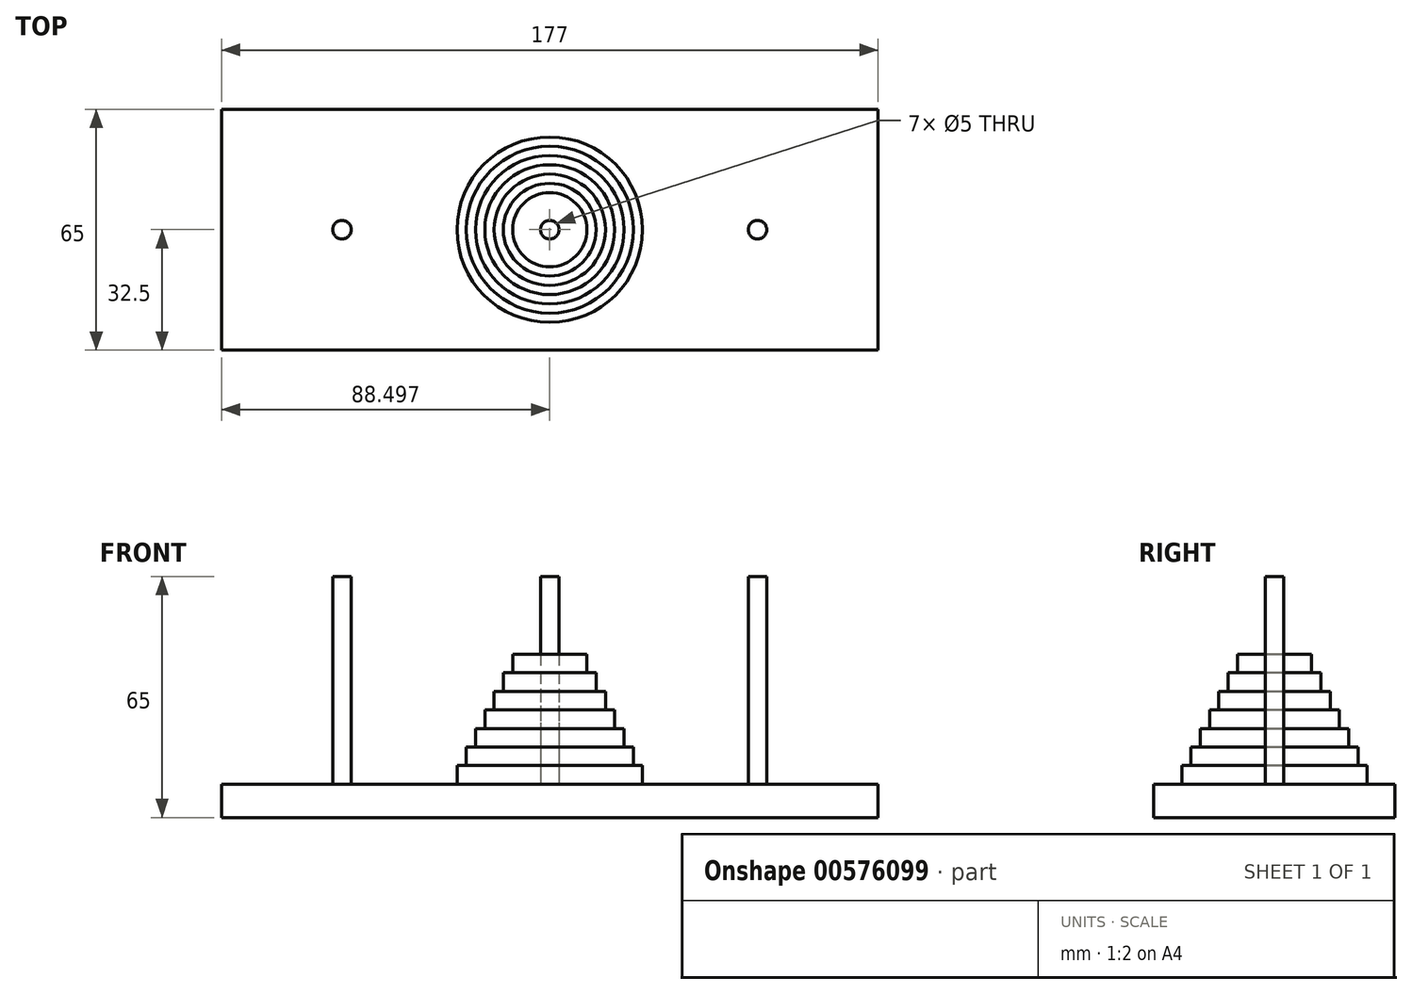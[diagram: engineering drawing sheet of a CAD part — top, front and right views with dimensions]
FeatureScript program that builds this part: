
annotation { "Feature Type Name" : "Feature", "Feature Type Description" : "" }
export const myFeature = defineFeature(function(context is Context, id is Id, definition is map)
    precondition{}
    {
        {
            var Q0;
            Q0=qCreatedBy(makeId("Front.planeOp"),FACE);
            var sketch = newSketch(context, id + "F0", { "sketchPlane" : qUnion([Q0])});
            skLineSegment(sketch, "E0", {"start": v(-126.76, 11.57) * mm, "end": v(50.24, 11.57) * mm});
            skLineSegment(sketch, "E1", {"start": v(50.24, 11.57) * mm, "end": v(50.24, 20.57) * mm});
            skLineSegment(sketch, "E2", {"start": v(50.24, 20.57) * mm, "end": v(-126.76, 20.57) * mm});
            skLineSegment(sketch, "E3", {"start": v(-126.76, 20.57) * mm, "end": v(-126.76, 11.57) * mm});
            skSolve(sketch);
        }
        {
            var Q0;
            Q0=makeQuery(id+"F0.imprint","IMPRINT",FACE,{"disambiguationData":[TD([[makeQuery(id+"F0.imprint","IMPRINT",EDGE,{"derivedFrom":sQuery(id+"F0.wireOp",EDGE,"E0")}),1.0]])]});
            extrude(context, id + "F1", {"entities" : qUnion([Q0]), "depth" : 65 * mm, "offsetDistance" : 25.4 * mm});
        }
        {
            var Q0;
            Q0=makeQuery(id+"F1.opExtrude","SWEPT_FACE",FACE,{"disambiguationData":[OSD([sQuery(id+"F0.wireOp",EDGE,"E2")])]});
            var sketch = newSketch(context, id + "F2", { "sketchPlane" : qUnion([Q0])});
            skLineSegment(sketch, "E4", {"start": v(20.24, -32.5) * mm, "end": v(17.74, -32.5) * mm});
            skLineSegment(sketch, "E5", {"start": v(17.74, -32.5) * mm, "end": v(15.24, -32.5) * mm});
            skLineSegment(sketch, "E6", {"start": v(-38.26, -32.5) * mm, "end": v(-40.76, -32.5) * mm});
            skLineSegment(sketch, "E7", {"start": v(-94.26, -32.5) * mm, "end": v(-96.76, -32.5) * mm});
            skCircle(sketch, "E8", {"center": v(-94.26, -32.5) * mm, "radius": 2.5 * mm});
            skCircle(sketch, "E9", {"center": v(-38.26, -32.5) * mm, "radius": 2.5 * mm});
            skCircle(sketch, "E10", {"center": v(17.74, -32.5) * mm, "radius": 2.5 * mm});
            skLineSegment(sketch, "E11.trimOffspring", {"start": v(-91.76, -32.5) * mm, "end": v(-94.26, -32.5) * mm});
            skPoint(sketch, "E12.orphan", {"position": v(-126.76, -32.5) * mm});
            skLineSegment(sketch, "E13.trimOffspring", {"start": v(-35.76, -32.5) * mm, "end": v(-38.26, -32.5) * mm});
            skPoint(sketch, "E14.orphan", {"position": v(50.24, -32.5) * mm});
            skSolve(sketch);
        }
        {
            var Q0;
            Q0 = qSketchRegion(id + "F2", true);
            extrude(context, id + "F3", {"entities" : qUnion([Q0]), "operationType" : NewBodyOperationType.ADD, "depth" : 56 * mm, "offsetDistance" : 25.4 * mm});
        }
        {
            var Q0;
            Q0=makeQuery(id+"F1.opExtrude","SWEPT_FACE",FACE,{"disambiguationData":[OSD([sQuery(id+"F0.wireOp",EDGE,"E2")])]});
            var sketch = newSketch(context, id + "F4", { "sketchPlane" : qUnion([Q0])});
            skCircle(sketch, "E15", {"center": v(-38.26, -32.5) * mm, "radius": 25 * mm});
            skLineSegment(sketch, "E16", {"start": v(-38.26, -32.5) * mm, "end": v(-38.26, -57.5) * mm});
            skLineSegment(sketch, "E17", {"start": v(-38.26, -57.5) * mm, "end": v(-38.26, -7.5) * mm});
            skSolve(sketch);
        }
        {
            var Q0;
            Q0=makeQuery(id+"F4.imprint","IMPRINT",FACE,{"disambiguationData":[TD([[makeQuery(id+"F4.imprint","IMPRINT",EDGE,{"derivedFrom":sQuery(id+"F4.wireOp",EDGE,"E15")}),1.0]])]});
            extrude(context, id + "F5", {"entities" : qUnion([Q0]), "depth" : 5 * mm, "offsetDistance" : 25.4 * mm});
        }
        {
            var Q0;
            Q0=makeQuery(id+"F5.opExtrude","CAP_FACE",FACE,{"disambiguationData":[OSD([sQuery(id+"F2.wireOp",EDGE,"E9"),sQuery(id+"F4.wireOp",EDGE,"E15")])],"isStart":false});
            var sketch = newSketch(context, id + "F6", { "sketchPlane" : qUnion([Q0])});
            skCircle(sketch, "E18", {"center": v(-38.26, -32.5) * mm, "radius": 22.5 * mm});
            skSolve(sketch);
        }
        {
            var Q0;
            Q0=makeQuery(id+"F6.imprint","IMPRINT",FACE,{"disambiguationData":[TD([[makeQuery(id+"F6.imprint","IMPRINT",EDGE,{"derivedFrom":sQuery(id+"F6.wireOp",EDGE,"E18")}),1.0]])]});
            extrude(context, id + "F7", {"entities" : qUnion([Q0]), "depth" : 5 * mm, "offsetDistance" : 25.4 * mm});
        }
        {
            var Q0;
            Q0=makeQuery(id+"F7.opExtrude","CAP_FACE",FACE,{"disambiguationData":[OSD([sQuery(id+"F2.wireOp",EDGE,"E9"),sQuery(id+"F6.wireOp",EDGE,"E18")])],"isStart":false});
            var sketch = newSketch(context, id + "F8", { "sketchPlane" : qUnion([Q0])});
            skCircle(sketch, "E19", {"center": v(-38.26, -32.5) * mm, "radius": 20 * mm});
            skSolve(sketch);
        }
        {
            var Q0;
            Q0=makeQuery(id+"F8.imprint","IMPRINT",FACE,{"disambiguationData":[TD([[makeQuery(id+"F8.imprint","IMPRINT",EDGE,{"derivedFrom":sQuery(id+"F8.wireOp",EDGE,"E19")}),1.0]])]});
            extrude(context, id + "F9", {"entities" : qUnion([Q0]), "depth" : 5 * mm, "offsetDistance" : 25.4 * mm});
        }
        {
            var Q0;
            Q0=makeQuery(id+"F9.opExtrude","CAP_FACE",FACE,{"disambiguationData":[OSD([sQuery(id+"F2.wireOp",EDGE,"E9"),sQuery(id+"F8.wireOp",EDGE,"E19")])],"isStart":false});
            var sketch = newSketch(context, id + "F10", { "sketchPlane" : qUnion([Q0])});
            skCircle(sketch, "E20", {"center": v(-38.26, -32.5) * mm, "radius": 17.5 * mm});
            skSolve(sketch);
        }
        {
            var Q0;
            Q0=makeQuery(id+"F10.imprint","IMPRINT",FACE,{"disambiguationData":[TD([[makeQuery(id+"F10.imprint","IMPRINT",EDGE,{"derivedFrom":sQuery(id+"F10.wireOp",EDGE,"E20")}),1.0]])]});
            extrude(context, id + "F11", {"entities" : qUnion([Q0]), "depth" : 5 * mm, "offsetDistance" : 25.4 * mm});
        }
        {
            var Q0;
            Q0=makeQuery(id+"F11.opExtrude","CAP_FACE",FACE,{"disambiguationData":[OSD([sQuery(id+"F2.wireOp",EDGE,"E9"),sQuery(id+"F10.wireOp",EDGE,"E20")])],"isStart":false});
            var sketch = newSketch(context, id + "F12", { "sketchPlane" : qUnion([Q0])});
            skCircle(sketch, "E21", {"center": v(-38.26, -32.5) * mm, "radius": 15 * mm});
            skSolve(sketch);
        }
        {
            var Q0;
            Q0=makeQuery(id+"F12.imprint","IMPRINT",FACE,{"disambiguationData":[TD([[makeQuery(id+"F12.imprint","IMPRINT",EDGE,{"derivedFrom":sQuery(id+"F12.wireOp",EDGE,"E21")}),1.0]])]});
            extrude(context, id + "F13", {"entities" : qUnion([Q0]), "depth" : 5 * mm, "offsetDistance" : 25.4 * mm});
        }
        {
            var Q0;
            Q0=makeQuery(id+"F13.opExtrude","CAP_FACE",FACE,{"disambiguationData":[OSD([sQuery(id+"F2.wireOp",EDGE,"E9"),sQuery(id+"F12.wireOp",EDGE,"E21")])],"isStart":false});
            var sketch = newSketch(context, id + "F14", { "sketchPlane" : qUnion([Q0])});
            skCircle(sketch, "E22", {"center": v(-38.26, -32.5) * mm, "radius": 12.5 * mm});
            skSolve(sketch);
        }
        {
            var Q0;
            Q0=makeQuery(id+"F14.imprint","IMPRINT",FACE,{"disambiguationData":[TD([[makeQuery(id+"F14.imprint","IMPRINT",EDGE,{"derivedFrom":sQuery(id+"F14.wireOp",EDGE,"E22")}),1.0]])]});
            extrude(context, id + "F15", {"entities" : qUnion([Q0]), "depth" : 5 * mm, "offsetDistance" : 25.4 * mm});
        }
        {
            var Q0;
            Q0=makeQuery(id+"F15.opExtrude","CAP_FACE",FACE,{"disambiguationData":[OSD([sQuery(id+"F2.wireOp",EDGE,"E9"),sQuery(id+"F14.wireOp",EDGE,"E22")])],"isStart":false});
            var sketch = newSketch(context, id + "F16", { "sketchPlane" : qUnion([Q0])});
            skCircle(sketch, "E23", {"center": v(-38.26, -32.5) * mm, "radius": 10 * mm});
            skSolve(sketch);
        }
        {
            var Q0;
            Q0=makeQuery(id+"F16.imprint","IMPRINT",FACE,{"disambiguationData":[TD([[makeQuery(id+"F16.imprint","IMPRINT",EDGE,{"derivedFrom":sQuery(id+"F16.wireOp",EDGE,"E23")}),1.0]])]});
            extrude(context, id + "F17", {"entities" : qUnion([Q0]), "depth" : 5 * mm, "offsetDistance" : 25.4 * mm});
        }
    });
